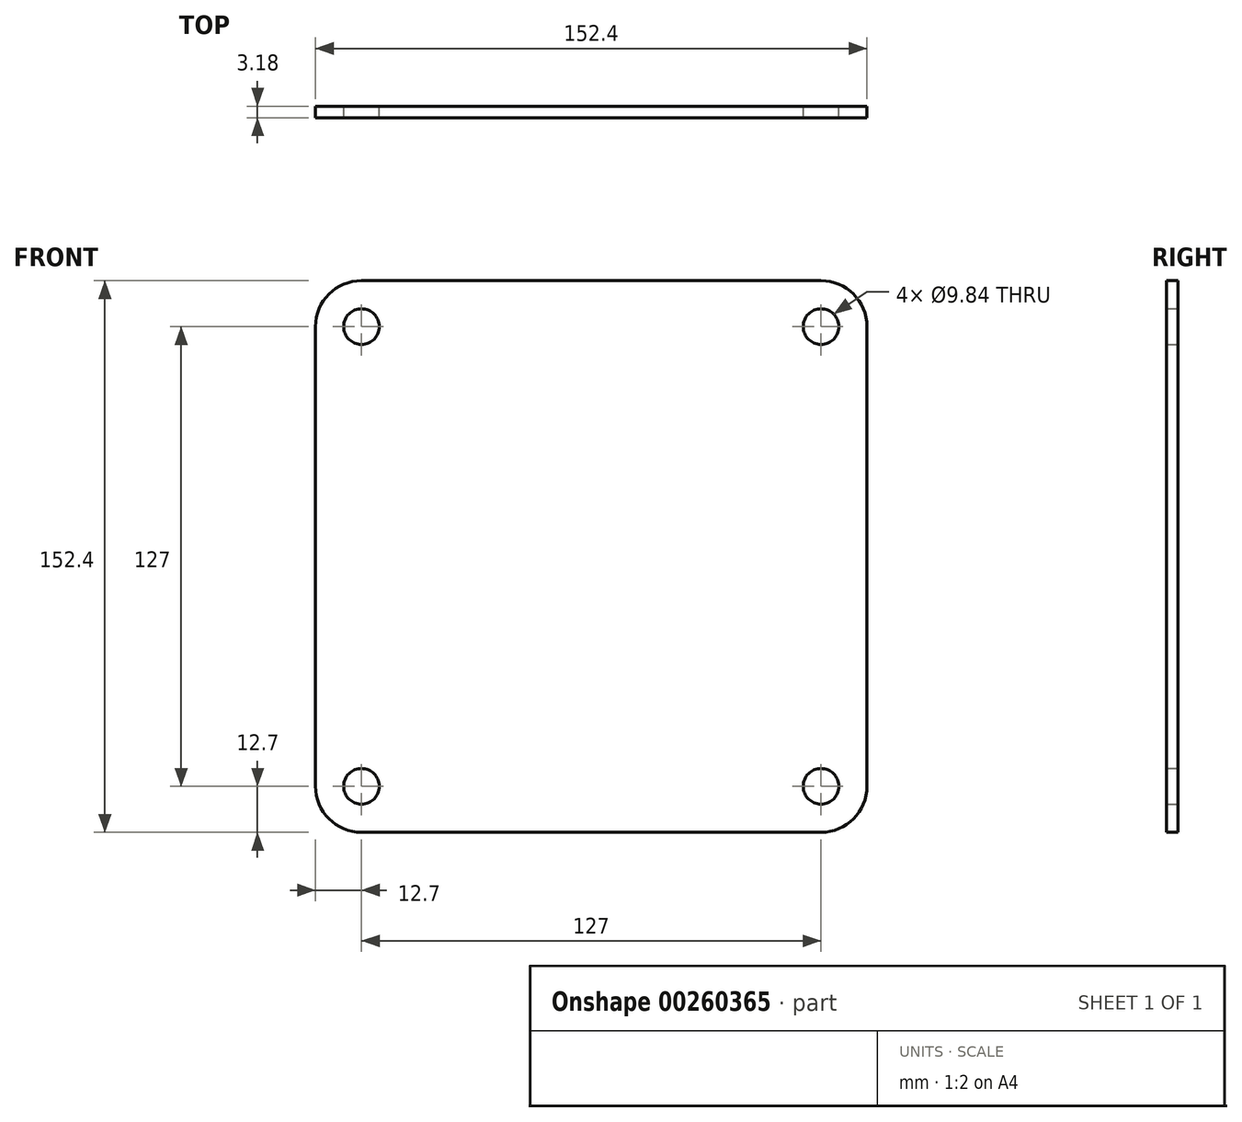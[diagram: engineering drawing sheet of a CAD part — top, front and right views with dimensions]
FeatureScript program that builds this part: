
annotation { "Feature Type Name" : "Feature", "Feature Type Description" : "" }
export const myFeature = defineFeature(function(context is Context, id is Id, definition is map)
    precondition{}
    {
        {
            var Q0;
            Q0=qCreatedBy(makeId("Front.planeOp"),FACE);
            var sketch = newSketch(context, id + "F0", { "sketchPlane" : qUnion([Q0])});
            skLineSegment(sketch, "E0.bottom", {"start": v(12.7, 0) * mm, "end": v(139.7, 0) * mm});
            skLineSegment(sketch, "E0.top", {"start": v(12.7, 152.4) * mm, "end": v(139.7, 152.4) * mm});
            skLineSegment(sketch, "E0.left", {"start": v(0, 12.7) * mm, "end": v(0, 139.7) * mm});
            skLineSegment(sketch, "E0.right", {"start": v(152.4, 12.7) * mm, "end": v(152.4, 139.7) * mm});
            skPoint(sketch, "E1.visualSharp", {"position": v(0, 152.4) * mm});
            skArc(sketch, "E1.filletArc", {"start": v(12.7, 152.4) * mm, "mid": v(3.72, 148.68) * mm, "end": v(0, 139.7) * mm});
            skPoint(sketch, "E2.visualSharp", {"position": v(152.4, 152.4) * mm});
            skArc(sketch, "E2.filletArc", {"start": v(152.4, 139.7) * mm, "mid": v(148.68, 148.68) * mm, "end": v(139.7, 152.4) * mm});
            skPoint(sketch, "E3.visualSharp", {"position": v(152.4, 0) * mm});
            skArc(sketch, "E3.filletArc", {"start": v(139.7, 0) * mm, "mid": v(148.68, 3.72) * mm, "end": v(152.4, 12.7) * mm});
            skPoint(sketch, "E4.visualSharp", {"position": v(0, 0) * mm});
            skArc(sketch, "E4.filletArc", {"start": v(0, 12.7) * mm, "mid": v(3.72, 3.72) * mm, "end": v(12.7, 0) * mm});
            skCircle(sketch, "E5", {"center": v(12.7, 139.7) * mm, "radius": 4.92 * mm});
            skCircle(sketch, "E6", {"center": v(139.7, 139.7) * mm, "radius": 4.92 * mm});
            skCircle(sketch, "E7", {"center": v(139.7, 12.7) * mm, "radius": 4.92 * mm});
            skCircle(sketch, "E8", {"center": v(12.7, 12.7) * mm, "radius": 4.92 * mm});
            skSolve(sketch);
        }
        {
            var Q0;
            Q0=makeQuery(id+"F0.imprint","IMPRINT",FACE,{"disambiguationData":[TD([[makeQuery(id+"F0.imprint","IMPRINT",EDGE,{"derivedFrom":sQuery(id+"F0.wireOp",EDGE,"E0.bottom")}),1.0]])]});
            extrude(context, id + "F1", {"entities" : qUnion([Q0]), "depth" : 3.17 * mm});
        }
    });
